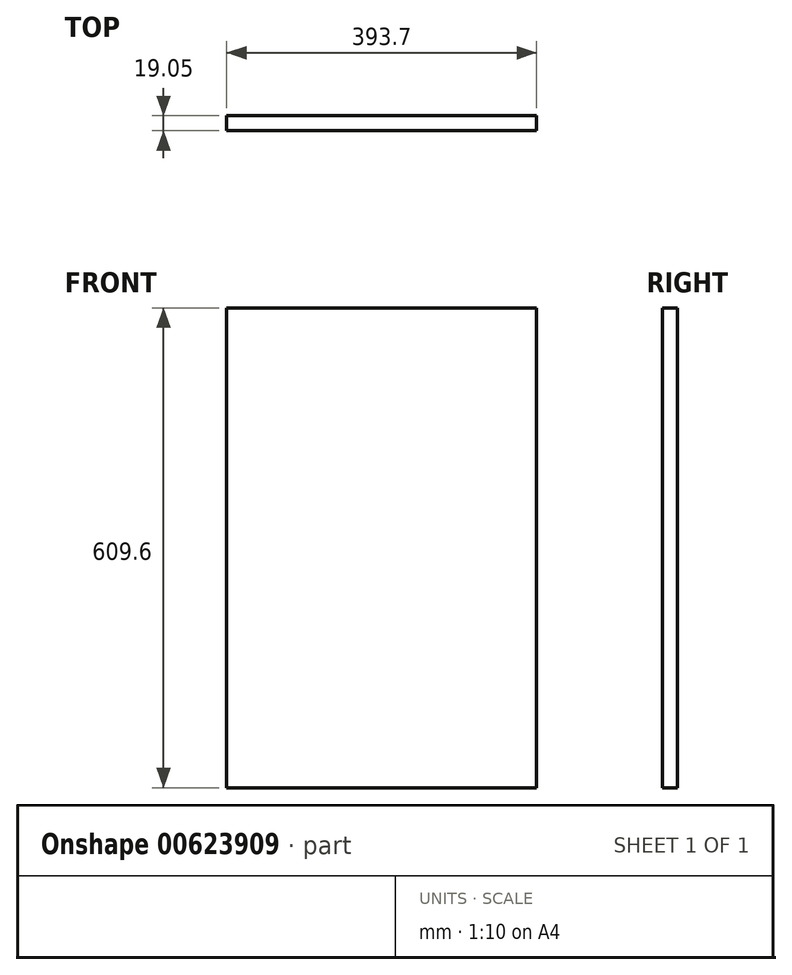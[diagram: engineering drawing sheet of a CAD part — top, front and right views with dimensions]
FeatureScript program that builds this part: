
annotation { "Feature Type Name" : "Feature", "Feature Type Description" : "" }
export const myFeature = defineFeature(function(context is Context, id is Id, definition is map)
    precondition{}
    {
        {
            var Q0;
            Q0=qCreatedBy(makeId("Front.planeOp"),FACE);
            var sketch = newSketch(context, id + "F0", { "sketchPlane" : qUnion([Q0])});
            skLineSegment(sketch, "E0.bottom", {"start": v(196.85, 304.8) * mm, "end": v(-196.85, 304.8) * mm});
            skLineSegment(sketch, "E0.top", {"start": v(196.85, -304.8) * mm, "end": v(-196.85, -304.8) * mm});
            skLineSegment(sketch, "E0.left", {"start": v(196.85, 304.8) * mm, "end": v(196.85, -304.8) * mm});
            skLineSegment(sketch, "E0.right", {"start": v(-196.85, 304.8) * mm, "end": v(-196.85, -304.8) * mm});
            skPoint(sketch, "E0.middle", {"position": v(0, 0) * mm});
            skSolve(sketch);
        }
        {
            var Q0;
            Q0=makeQuery(id+"F0.imprint","IMPRINT",FACE,{"disambiguationData":[TD([[makeQuery(id+"F0.imprint","IMPRINT",EDGE,{"derivedFrom":sQuery(id+"F0.wireOp",EDGE,"E0.bottom")}),1.0]])]});
            extrude(context, id + "F1", {"entities" : qUnion([Q0]), "depth" : 19.05 * mm, "offsetDistance" : 25.4 * mm});
        }
    });
